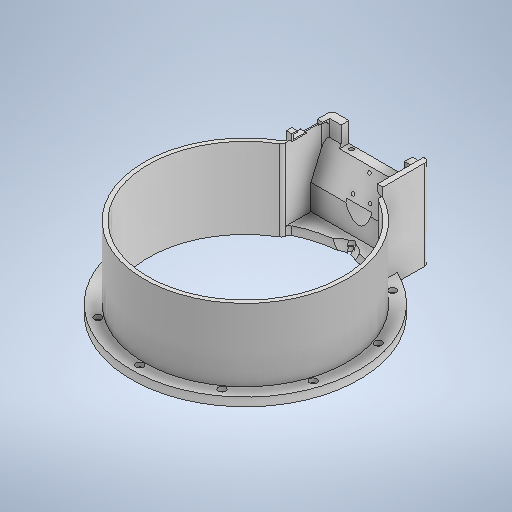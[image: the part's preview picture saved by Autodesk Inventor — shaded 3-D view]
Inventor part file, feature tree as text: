
AUTODESK INVENTOR PART (.ipt)
format: ipt  version: 2025.2 (Build 292293000, 293)  size: 745,984 bytes
history: native  units: in
note: dims shown in document units (in); Inventor stores cm internally (conversion verified against a paired STEP export)
features: extrude x27, sketch x24, other x3, plane x3, chamfer x3, fillet x1
ambient origin geometry x8: Origin, YZ Plane, XZ Plane, XY Plane, X Axis, Y Axis, Z Axis, Center Point
bodies: Body1 (feature_tree)
feature tree (61):
  other  "Cylinder.ipt"
  extrude  "Extrusion1"  Depth=0.3937in
  extrude  "Extrusion2"  Depth=0.3937in TaperAngle=0.0deg
  sketch  "Sketch3"  dims[d7=11.2205in d8=10.6299in]
  extrude  "Extrusion3"  Depth=10.6299in
  extrude  "Extrusion5"  Depth=0.1969in TaperAngle=0.0deg
  sketch  "Sketch6"  dims[d24=0.1969in d25=0.0in d31=0.0in d32=0.0in]
  extrude  "Extrusion6"  Depth=10.6299in
  extrude  "Extrusion7"  TaperAngle=0.0deg  [1 undecoded]
  extrude  "Extrusion8"  Depth=9.8425in
  plane  "Work Plane1"
  extrude  "Extrusion9"  Depth=10.6299in
  extrude  "Extrusion21"  Depth=0.0787in
  sketch  "Sketch19"  dims[d107=2.2047in d108=0.0in d113=2.5591in]
  extrude  "Extrusion34"  Depth=2.5591in
  extrude  "Extrusion43"  Depth=0.0591in
  extrude  "Extrusion53"  Depth=0.0787in
  extrude  "Extrusion44"  Depth=0.0787in
  extrude  "Extrusion45"  TaperAngle=90.0deg  [1 undecoded]
  chamfer  "Chamfer8"  Distance=1.1614in
  sketch  "Sketch31"  dims[d164=1.5298in d165=0.0787in]
  extrude  "Extrusion46"  Depth=0.0787in
  extrude  "Extrusion47"  Depth=3.937in TaperAngle=360.0deg
  plane  "Work Plane2"
  extrude  "Extrusion48"  Depth=9.065in
  plane  "Work Plane3"
  extrude  "Extrusion51"  Depth=1.8228in
  extrude  "Extrusion54"  Depth=2.564in
  extrude  "Extrusion55"  Depth=3.5433in
  extrude  "Extrusion56"  Depth=3.3661in TaperAngle=0.0deg
  extrude  "Extrusion57"  Depth=3.1496in TaperAngle=0.0deg
  extrude  "Extrusion58"  Depth=0.0787in
  extrude  "Extrusion59"  Depth=0.1575in
  extrude  "Extrusion60"  Depth=0.1575in
  extrude  "Extrusion61"  Depth=0.0787in
  extrude  "Extrusion62"  Depth=0.0787in
  fillet  "Fillet22"  Radius=0.4331in
  chamfer  "Chamfer12"  Distance=0.4331in
  chamfer  "Chamfer13"  Distance=2.1654in
  other  "Solid12::Cylinder.ipt"
  other  "TaggingFeature1"
  sketch  "Sketch1"  dims[d0=0.3937in d2=10.2362in]
  sketch  "Sketch2"  dims[d3=0.0in d4=0.0in d5=0.3937in d6=0.0in]
  sketch  "Sketch5"  dims[d17=10.6299in d18=0.2953in]
  sketch  "Sketch7"  dims[d33=2.1654in d34=0.0in d35=9.8425in]
  sketch  "Sketch9"  dims[d36=10.6299in d46=9.065in]
  sketch  "Sketch14"  dims[d47=0.3937in d48=0.0in d88=0.0787in]
  sketch  "Sketch22"  dims[d117=0.0591in d120=0.5433in]
  sketch  "Sketch Circular Pattern3"  dims[d10=0.1969in d11=0.0in d15=0.1969in d16=0.0in]
  sketch  "Sketch30"  dims[d122=9.4488in d134=0.0787in]
  sketch  "Sketch32"  dims[d166=1.8325in d167=90.0deg d173=1.1614in d174=0.0in]
  sketch  "Sketch35"  dims[d175=0.0787in d209=0.2165in]
  sketch  "Sketch37"  dims[d210=0.3425in d211=3.937in d213=360.0deg]
  sketch  "Sketch38"  dims[d217=10.4151in d218=9.065in]
  sketch  "Sketch39"  dims[d223=0.5433in d224=1.8228in]
  sketch  "Sketch40"  dims[d225=3.5433in d226=2.564in]
  sketch  "Sketch42"  dims[d227=2.7608in d228=3.5433in]
  sketch  "Sketch43"  dims[d233=7.3568in d234=1.5846in d235=0.0in d236=0.0in d237=3.3661in d238=0.3937in d239=0.0in d240=0.0in]
  sketch  "Sketch45"  dims[d241=0.9843in d242=3.1496in d243=0.0in]
  sketch  "Sketch46"  dims[d244=1.5748in d245=0.0787in d246=0.1598in d247=0.4331in]
  sketch  "Sketch47"  dims[d248=0.1575in d249=0.1575in d250=0.1575in d251=0.9331in d255=0.9331in d256=0.4331in d257=0.4331in d258=2.1654in d259=0.0in d260=0.1772in d261=0.0in d263=0.1666in d265=1.5871in d266=0.0in d267=1.5748in d268=0.5315in d269=-3.5433in d277=2.9528in d279=1.5787in d280=0.0in d293=1.378in d306=4.5276in d307=0.0591in d308=2.7608in d309=3.5433in d311=0.3937in d312=0.3937in d313=3.3661in d314=0.3937in d315=0.0in d316=0.0in d317=1.5871in d318=0.0in d319=0.1969in d320=1.1811in d321=0.5906in d322=0.0in d323=0.3937in d324=0.0in d327=0.1772in d328=1.5871in d329=0.0in d330=0.1575in d331=0.0in d332=0.0591in d333=0.1969in d334=0.0in d335=0.2559in d336=0.0in d337=0.0591in d338=0.0591in d339=0.1768in d340=0.0in d341=0.7874in d342=0.0591in d343=0.0591in d344=0.1969in d345=0.0in d346=0.2559in d347=0.0591in d348=0.2559in d349=0.0591in d350=0.1969in d351=0.0in d352=0.1969in d353=0.1575in d354=0.0787in d355=45.0deg d356=0.0787in d357=0.0787in d358=45.0deg d143=0.0197in d144=0.0344in d145=0.0197in d146=0.0344in d153=0.0in d154=0.0in d155=0.0in d156=0.0in d201=0.0197in d202=0.0344in d203=0.0197in d204=0.0344in d215=0.0197in d216=0.0344in d294=0.0197in d295=0.0344in d296=0.0197in d297=0.0344in]
note: 2 required parameter values undecoded (feature->parameter linkage not recoverable at this tier; creation-order binding heuristic only, values carry confidence <= 0.55)
